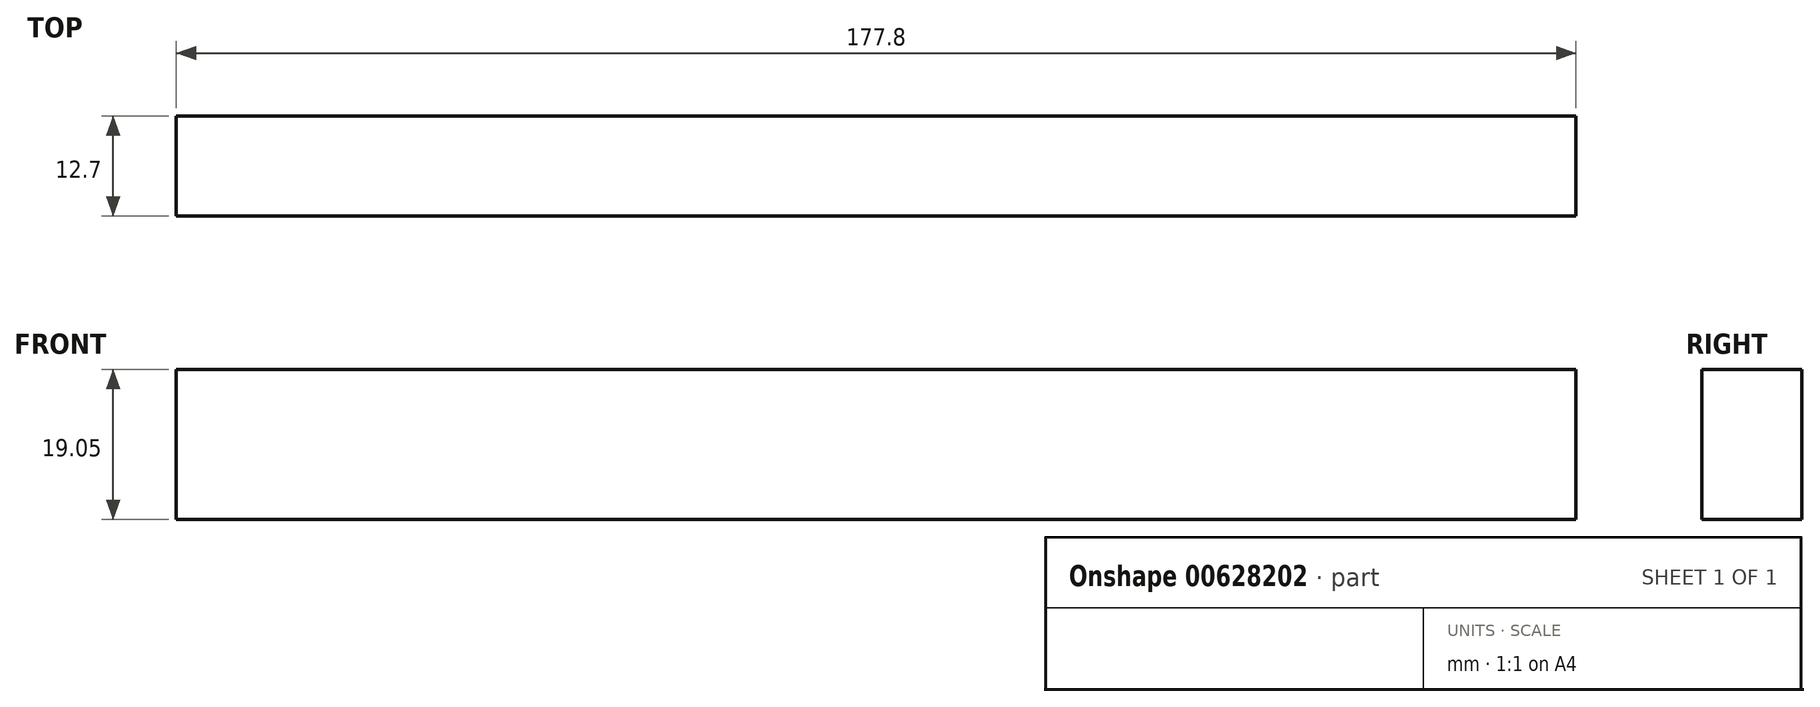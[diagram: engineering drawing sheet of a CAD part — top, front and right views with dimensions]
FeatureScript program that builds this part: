
annotation { "Feature Type Name" : "Feature", "Feature Type Description" : "" }
export const myFeature = defineFeature(function(context is Context, id is Id, definition is map)
    precondition{}
    {
        {
            var Q0;
            Q0=qCreatedBy(makeId("Front.planeOp"),FACE);
            var sketch = newSketch(context, id + "F0", { "sketchPlane" : qUnion([Q0])});
            skLineSegment(sketch, "E0.bottom", {"start": v(0, 0) * mm, "end": v(177.8, 0) * mm});
            skLineSegment(sketch, "E0.top", {"start": v(0, 19.05) * mm, "end": v(177.8, 19.05) * mm});
            skLineSegment(sketch, "E0.left", {"start": v(0, 0) * mm, "end": v(0, 19.05) * mm});
            skLineSegment(sketch, "E0.right", {"start": v(177.8, 0) * mm, "end": v(177.8, 19.05) * mm});
            skSolve(sketch);
        }
        {
            var Q0;
            Q0=qSketchRegion(id+"F0",true);
            extrude(context, id + "F1", {"entities" : qUnion([Q0]), "depth" : 12.7 * mm, "offsetDistance" : 25.4 * mm});
        }
    });
